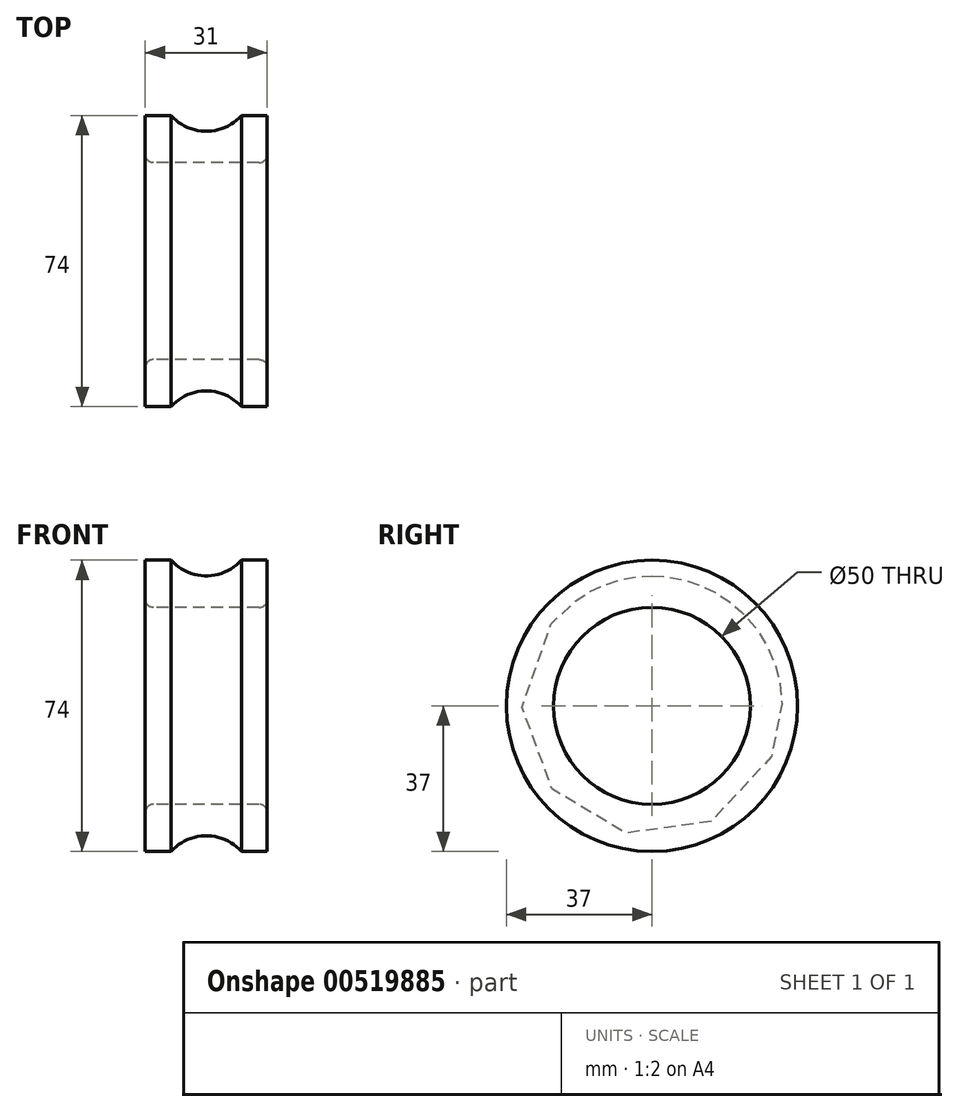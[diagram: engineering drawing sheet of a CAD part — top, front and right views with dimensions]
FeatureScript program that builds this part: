
annotation { "Feature Type Name" : "Feature", "Feature Type Description" : "" }
export const myFeature = defineFeature(function(context is Context, id is Id, definition is map)
    precondition{}
    {
        {
            var Q0;
            Q0=qCreatedBy(makeId("Top.planeOp"),FACE);
            var sketch = newSketch(context, id + "F0", { "sketchPlane" : qUnion([Q0])});
            skLineSegment(sketch, "E0", {"start": v(-25.09, 0) * mm, "end": v(22.8, 0) * mm, "construction": true});
            skLineSegment(sketch, "E1.bottom", {"start": v(-15.5, 37) * mm, "end": v(-8.94, 37) * mm});
            skLineSegment(sketch, "E1.top", {"start": v(-15.5, 25) * mm, "end": v(15.5, 25) * mm});
            skLineSegment(sketch, "E1.left", {"start": v(-15.5, 37) * mm, "end": v(-15.5, 25) * mm});
            skLineSegment(sketch, "E1.right", {"start": v(15.5, 37) * mm, "end": v(15.5, 25) * mm});
            skPoint(sketch, "E1.middle", {"position": v(0, 31) * mm});
            skLineSegment(sketch, "E2", {"start": v(0, 0) * mm, "end": v(0, 25) * mm, "construction": true});
            skArc(sketch, "E3", {"start": v(-8.94, 37) * mm, "mid": v(0, 33) * mm, "end": v(8.94, 37) * mm});
            skLineSegment(sketch, "E4.trimOffspring", {"start": v(8.94, 37) * mm, "end": v(15.5, 37) * mm});
            skSolve(sketch);
        }
        {
            var Q0;
            Q0=makeQuery(id+"F0.imprint","IMPRINT",FACE,{"disambiguationData":[TD([[makeQuery(id+"F0.imprint","IMPRINT",EDGE,{"derivedFrom":sQuery(id+"F0.wireOp",EDGE,"E1.bottom")}),-1.0]])]});
            var Q1;
            Q1=sQuery(id+"F0.wireOp",EDGE,"E0");
            revolve(context, id + "F1", {"entities" : qUnion([Q0]), "axis" : qUnion([Q1]), "revolveType" : RevolveType.FULL});
        }
        {
            var Q0;
            Q0=makeQuery(id+"F1.opRevolve","SWEPT_EDGE",EDGE,{"disambiguationData":[OSD([sQuery(id+"F0.wireOp",EDGE,"E1.top"),sQuery(id+"F0.wireOp",EDGE,"E1.right")])]});
            var Q1;
            Q1=makeQuery(id+"F1.opRevolve","SWEPT_EDGE",EDGE,{"disambiguationData":[OSD([sQuery(id+"F0.wireOp",EDGE,"E1.top"),sQuery(id+"F0.wireOp",EDGE,"E1.left")])]});
            fillet(context, id + "F2", {"entities" : qUnion([Q0, Q1]), "radius" : 2.1 * mm, "tangentPropagation" : true, "allowEdgeOverflow" : false});
        }
    });
